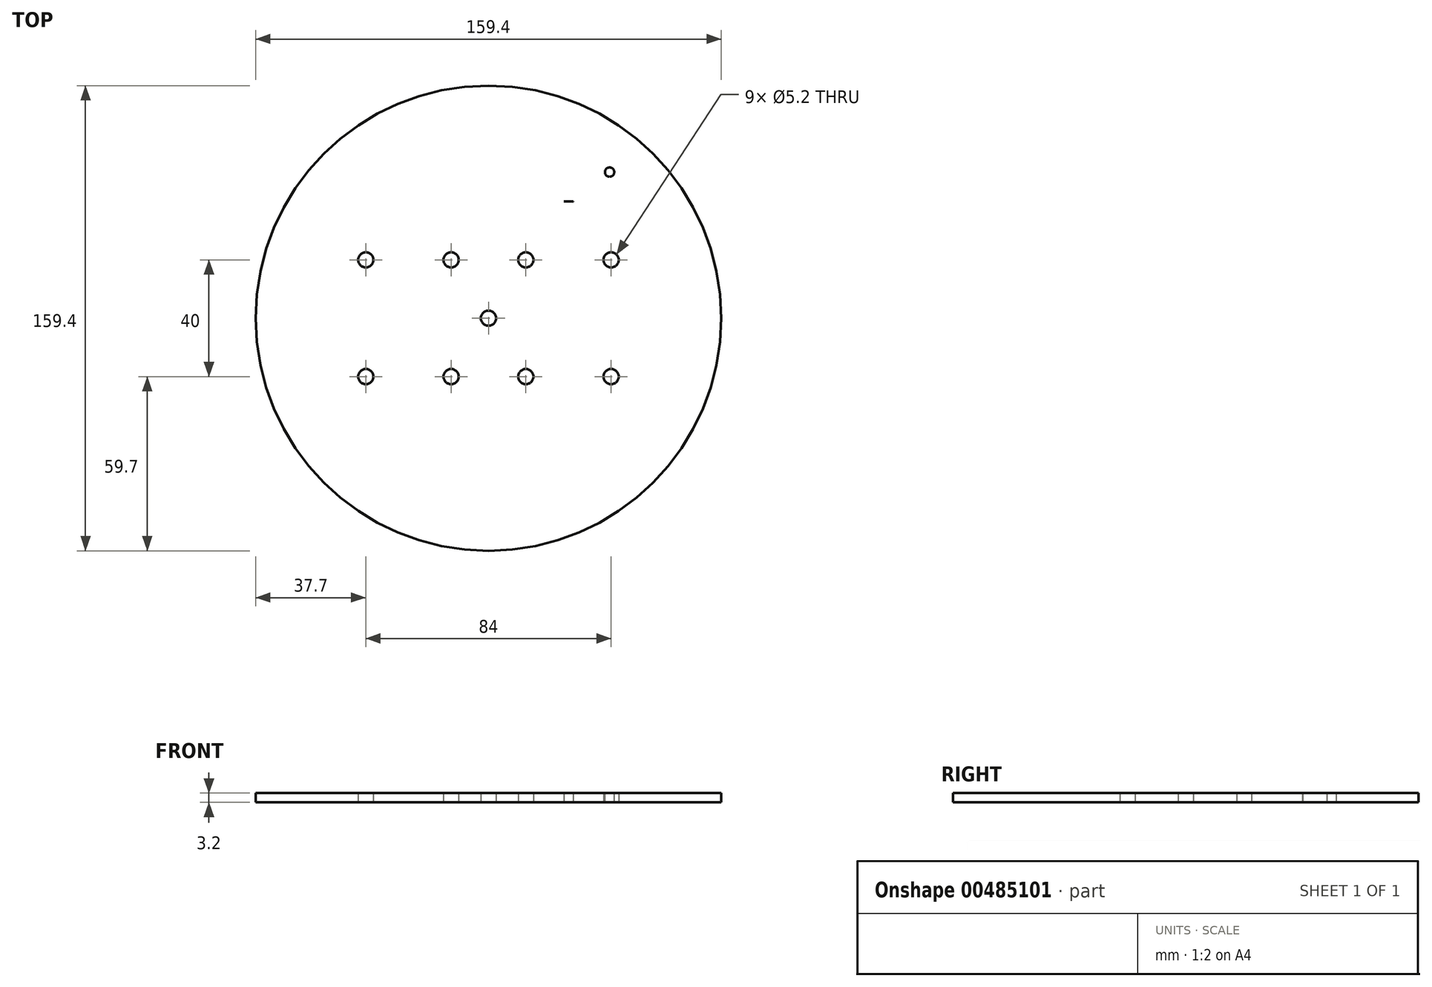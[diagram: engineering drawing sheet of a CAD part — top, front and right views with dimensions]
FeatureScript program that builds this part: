
annotation { "Feature Type Name" : "Feature", "Feature Type Description" : "" }
export const myFeature = defineFeature(function(context is Context, id is Id, definition is map)
    precondition{}
    {
        {
            var Q0;
            Q0=qCreatedBy(makeId("Top.planeOp"),FACE);
            var sketch = newSketch(context, id + "F0", { "sketchPlane" : qUnion([Q0])});
            skCircle(sketch, "E0", {"center": v(0, 0) * mm, "radius": 79.7 * mm});
            skLineSegment(sketch, "E1", {"start": v(-68.94, 40) * mm, "end": v(68.94, 40) * mm, "construction": true});
            skLineSegment(sketch, "E2", {"start": v(-68.94, -40) * mm, "end": v(68.94, -40) * mm, "construction": true});
            skLineSegment(sketch, "E3", {"start": v(-79.7, 0) * mm, "end": v(79.7, 0) * mm, "construction": true});
            skLineSegment(sketch, "E4", {"start": v(-29, 40) * mm, "end": v(-29, -40) * mm, "construction": true});
            skLineSegment(sketch, "E5", {"start": v(-25.8, 40) * mm, "end": v(-25.8, -40) * mm, "construction": true});
            skLineSegment(sketch, "E6", {"start": v(25.8, 40) * mm, "end": v(25.8, -40) * mm, "construction": true});
            skLineSegment(sketch, "E7", {"start": v(29, 39.93) * mm, "end": v(29, -40) * mm, "construction": true});
            skLineSegment(sketch, "E8", {"start": v(0, 40) * mm, "end": v(0, -40) * mm, "construction": true});
            skLineSegment(sketch, "E9", {"start": v(-29, 40) * mm, "end": v(-29, -40) * mm});
            skLineSegment(sketch, "E10", {"start": v(-25.8, -40) * mm, "end": v(-25.8, 40) * mm});
            skLineSegment(sketch, "E11", {"start": v(-29, 40) * mm, "end": v(-25.8, 40) * mm});
            skLineSegment(sketch, "E12", {"start": v(-25.8, -40) * mm, "end": v(-29, -40) * mm});
            skLineSegment(sketch, "E13", {"start": v(25.8, -40) * mm, "end": v(29, -40) * mm});
            skLineSegment(sketch, "E14", {"start": v(29, 39.93) * mm, "end": v(25.8, 40) * mm});
            skLineSegment(sketch, "E15", {"start": v(25.8, 40) * mm, "end": v(25.8, -40) * mm});
            skLineSegment(sketch, "E16", {"start": v(29, -40) * mm, "end": v(29, 39.93) * mm});
            skLineSegment(sketch, "E17", {"start": v(-29, 0) * mm, "end": v(-25.8, 0) * mm, "construction": true});
            skLineSegment(sketch, "E18", {"start": v(25.8, 0) * mm, "end": v(29, 0) * mm, "construction": true});
            skLineSegment(sketch, "E19", {"start": v(-29, -20) * mm, "end": v(29, -20) * mm, "construction": true});
            skLineSegment(sketch, "E20", {"start": v(-29, 20) * mm, "end": v(29, 20) * mm, "construction": true});
            skLineSegment(sketch, "E21", {"start": v(-29, 0) * mm, "end": v(-42, 0) * mm, "construction": true});
            skLineSegment(sketch, "E22", {"start": v(-29, 20) * mm, "end": v(-77.15, 20) * mm, "construction": true});
            skLineSegment(sketch, "E23", {"start": v(-29, -20) * mm, "end": v(-77.15, -20) * mm, "construction": true});
            skLineSegment(sketch, "E24", {"start": v(-42, 20) * mm, "end": v(-42, -20) * mm, "construction": true});
            skLineSegment(sketch, "E25", {"start": v(29, 20) * mm, "end": v(77.15, 20) * mm, "construction": true});
            skLineSegment(sketch, "E26", {"start": v(29, -20) * mm, "end": v(77.15, -20) * mm, "construction": true});
            skLineSegment(sketch, "E27", {"start": v(42, 20) * mm, "end": v(42, -20) * mm, "construction": true});
            skCircle(sketch, "E28", {"center": v(-42, 20) * mm, "radius": 2.6 * mm});
            skCircle(sketch, "E29", {"center": v(-42, -20) * mm, "radius": 2.6 * mm});
            skCircle(sketch, "E30", {"center": v(42, 20) * mm, "radius": 2.6 * mm});
            skCircle(sketch, "E31", {"center": v(42, -20) * mm, "radius": 2.6 * mm});
            skLineSegment(sketch, "E32", {"start": v(-12.8, 20) * mm, "end": v(-12.8, -20) * mm, "construction": true});
            skLineSegment(sketch, "E33", {"start": v(12.8, 20) * mm, "end": v(12.8, -20) * mm, "construction": true});
            skPoint(sketch, "E34", {"position": v(-25.8, 20) * mm});
            skPoint(sketch, "E35", {"position": v(25.8, 20) * mm});
            skCircle(sketch, "E36", {"center": v(-12.8, 20) * mm, "radius": 2.6 * mm});
            skCircle(sketch, "E37", {"center": v(12.8, 20) * mm, "radius": 2.6 * mm});
            skCircle(sketch, "E38", {"center": v(-12.8, -20) * mm, "radius": 2.6 * mm});
            skCircle(sketch, "E39", {"center": v(12.8, -20) * mm, "radius": 2.6 * mm});
            skLineSegment(sketch, "E40.top", {"start": v(-29, -40) * mm, "end": v(-25.8, -40) * mm});
            skLineSegment(sketch, "E40.right", {"start": v(-25.8, 40) * mm, "end": v(-25.8, -40) * mm});
            skLineSegment(sketch, "E41.bottom", {"start": v(25.8, 40) * mm, "end": v(29, 40) * mm});
            skLineSegment(sketch, "E41.right", {"start": v(29, 40) * mm, "end": v(29, -40) * mm});
            skCircle(sketch, "E42", {"center": v(0, 0) * mm, "radius": 2.6 * mm});
            skSolve(sketch);
        }
        {
            var Q0;
            Q0=makeQuery(id+"F0.imprint","IMPRINT",FACE,{"disambiguationData":[TD([[makeQuery(id+"F0.imprint","IMPRINT",EDGE,{"derivedFrom":sQuery(id+"F0.wireOp",EDGE,"E9")}),1.0]])]});
            var Q1;
            Q1=makeQuery(id+"F0.imprint","IMPRINT",FACE,{"disambiguationData":[TD([[makeQuery(id+"F0.imprint","IMPRINT",EDGE,{"derivedFrom":sQuery(id+"F0.wireOp",EDGE,"E13")}),1.0]])]});
            var Q2;
            Q2=makeQuery(id+"F0.imprint","IMPRINT",FACE,{"disambiguationData":[TD([[makeQuery(id+"F0.imprint","IMPRINT",EDGE,{"derivedFrom":sQuery(id+"F0.wireOp",EDGE,"E0")}),1.0]])]});
            extrude(context, id + "F1", {"entities" : qUnion([Q0, Q1, Q2]), "depth" : 3.2 * mm, "offsetDistance" : 25 * mm});
        }
        {
            var Q0;
            Q0=makeQuery(id+"F0.imprint","IMPRINT",FACE,{"disambiguationData":[TD([[makeQuery(id+"F0.imprint","IMPRINT",EDGE,{"derivedFrom":sQuery(id+"F0.wireOp",EDGE,"E11")}),-1.0]])]});
            var Q1;
            {var subQ0=sQuery(id+"F0.wireOp",EDGE,"E14");Q1=makeQuery(id+"F0.imprint","IMPRINT",FACE,{"disambiguationData":[TD([[makeQuery(id+"F0.imprint","IMPRINT",EDGE,{"derivedFrom":subQ0}),1.0]])]});}
            extrude(context, id + "F2", {"entities" : qUnion([Q0, Q1]), "operationType" : NewBodyOperationType.ADD, "depth" : 3 * mm, "offsetDistance" : 25 * mm});
        }
        {
            var Q0;
            Q0=makeQuery(id+"F1.opExtrude","CAP_FACE",FACE,{"disambiguationData":[OSD([sQuery(id+"F0.wireOp",EDGE,"E0"),sQuery(id+"F0.wireOp",EDGE,"E28"),sQuery(id+"F0.wireOp",EDGE,"E29"),sQuery(id+"F0.wireOp",EDGE,"E30"),sQuery(id+"F0.wireOp",EDGE,"E31"),sQuery(id+"F0.wireOp",EDGE,"E36"),sQuery(id+"F0.wireOp",EDGE,"E37"),sQuery(id+"F0.wireOp",EDGE,"E38"),sQuery(id+"F0.wireOp",EDGE,"E39"),sQuery(id+"F0.wireOp",EDGE,"E11"),sQuery(id+"F0.wireOp",EDGE,"E40.top"),sQuery(id+"F0.wireOp",EDGE,"E9"),sQuery(id+"F0.wireOp",EDGE,"E40.right"),sQuery(id+"F0.wireOp",EDGE,"E41.bottom"),sQuery(id+"F0.wireOp",EDGE,"E13"),sQuery(id+"F0.wireOp",EDGE,"E15"),sQuery(id+"F0.wireOp",EDGE,"E41.right"),sQuery(id+"F0.wireOp",EDGE,"E42")])],"isStart":false});
            var sketch = newSketch(context, id + "F3", { "sketchPlane" : qUnion([Q0])});
            skCircle(sketch, "E43", {"center": v(0, 0) * mm, "radius": 65 * mm, "construction": true});
            skCircle(sketch, "E44", {"center": v(-33.9, -55.47) * mm, "radius": 1.6 * mm, "construction": true});
            skCircle(sketch, "E45", {"center": v(41.47, 50.05) * mm, "radius": 1.6 * mm, "construction": true});
            skSolve(sketch);
        }
        {
            var Q0;
            Q0=sQuery(id+"F3.wireOp",VERTEX,"E45.center");
            var Q1;
            Q1=makeQuery(id+"F1.opExtrude","SWEPT_BODY",BODY,{"disambiguationData":[OSD([sQuery(id+"F0.wireOp",EDGE,"E0"),sQuery(id+"F0.wireOp",EDGE,"E28"),sQuery(id+"F0.wireOp",EDGE,"E29"),sQuery(id+"F0.wireOp",EDGE,"E30"),sQuery(id+"F0.wireOp",EDGE,"E31"),sQuery(id+"F0.wireOp",EDGE,"E36"),sQuery(id+"F0.wireOp",EDGE,"E37"),sQuery(id+"F0.wireOp",EDGE,"E38"),sQuery(id+"F0.wireOp",EDGE,"E39"),sQuery(id+"F0.wireOp",EDGE,"E11"),sQuery(id+"F0.wireOp",EDGE,"E40.top"),sQuery(id+"F0.wireOp",EDGE,"E9"),sQuery(id+"F0.wireOp",EDGE,"E40.right"),sQuery(id+"F0.wireOp",EDGE,"E41.bottom"),sQuery(id+"F0.wireOp",EDGE,"E13"),sQuery(id+"F0.wireOp",EDGE,"E15"),sQuery(id+"F0.wireOp",EDGE,"E41.right"),sQuery(id+"F0.wireOp",EDGE,"E42")])]});
            hole(context, id + "F4", {"style" : HoleStyle.SIMPLE, "endStyle" : HoleEndStyle.BLIND, "holeDiameter" : 3.2 * mm, "holeDepth" : 3.2 * mm, "isTappedThrough" : true, "tappedDepth" : 12 * mm, "tapClearance" : 3, "locations" : qUnion([Q0]), "scope" : qUnion([Q1])});
        }
    });
